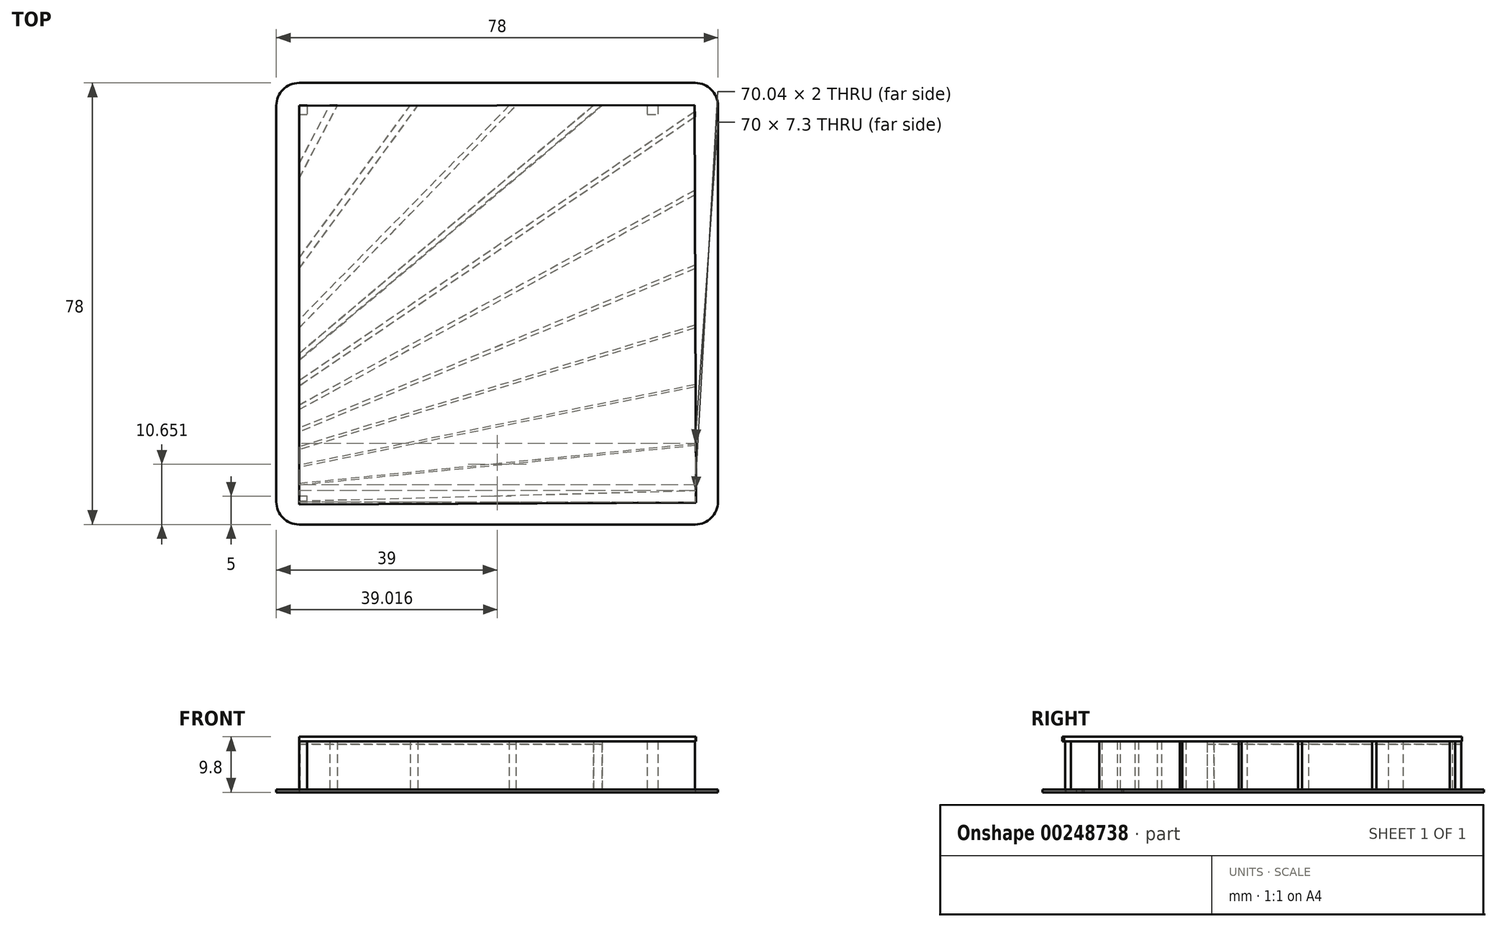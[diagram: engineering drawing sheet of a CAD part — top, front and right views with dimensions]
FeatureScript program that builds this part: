
annotation { "Feature Type Name" : "Feature", "Feature Type Description" : "" }
export const myFeature = defineFeature(function(context is Context, id is Id, definition is map)
    precondition{}
    {
        {
            var Q0;
            Q0=qCreatedBy(makeId("Top.planeOp"),FACE);
            var sketch = newSketch(context, id + "F0", { "sketchPlane" : qUnion([Q0])});
            skLineSegment(sketch, "E0.bottom", {"start": v(4, 78) * mm, "end": v(74, 78) * mm});
            skLineSegment(sketch, "E0.top", {"start": v(4, 0) * mm, "end": v(74, 0) * mm});
            skLineSegment(sketch, "E0.left", {"start": v(0, 74) * mm, "end": v(0, 4) * mm});
            skLineSegment(sketch, "E0.right", {"start": v(78, 74) * mm, "end": v(78, 4) * mm});
            skPoint(sketch, "E1.visualSharp", {"position": v(0, 0) * mm});
            skArc(sketch, "E1.filletArc", {"start": v(0, 4) * mm, "mid": v(1.17, 1.17) * mm, "end": v(4, 0) * mm});
            skPoint(sketch, "E2.visualSharp", {"position": v(0, 78) * mm});
            skArc(sketch, "E2.filletArc", {"start": v(4, 78) * mm, "mid": v(1.17, 76.83) * mm, "end": v(0, 74) * mm});
            skPoint(sketch, "E3.visualSharp", {"position": v(78, 0) * mm});
            skArc(sketch, "E3.filletArc", {"start": v(74, 0) * mm, "mid": v(76.83, 1.17) * mm, "end": v(78, 4) * mm});
            skPoint(sketch, "E4.visualSharp", {"position": v(78, 78) * mm});
            skArc(sketch, "E4.filletArc", {"start": v(78, 74) * mm, "mid": v(76.83, 76.83) * mm, "end": v(74, 78) * mm});
            skLineSegment(sketch, "E5.bottom", {"start": v(4, 4) * mm, "end": v(74.03, 4) * mm});
            skLineSegment(sketch, "E5.left", {"start": v(4, 4) * mm, "end": v(4, 4.15) * mm});
            skLineSegment(sketch, "E5.right", {"start": v(74.03, 4) * mm, "end": v(74, 6) * mm});
            skLineSegment(sketch, "E6", {"start": v(4, 4.15) * mm, "end": v(74, 6) * mm});
            skLineSegment(sketch, "E7", {"start": v(4, 7) * mm, "end": v(74, 14) * mm});
            skLineSegment(sketch, "E8", {"start": v(74.03, 4) * mm, "end": v(73.8, 70.2) * mm, "construction": true});
            skLineSegment(sketch, "E9", {"start": v(4, 4) * mm, "end": v(4, 69.95) * mm, "construction": true});
            skLineSegment(sketch, "E10.0", {"start": v(4, 7.3) * mm, "end": v(74, 14.3) * mm});
            skLineSegment(sketch, "E11", {"start": v(4, 7) * mm, "end": v(4, 7.3) * mm});
            skLineSegment(sketch, "E12", {"start": v(74, 14) * mm, "end": v(74, 14.3) * mm});
            skLineSegment(sketch, "E13", {"start": v(36.58, 10.26) * mm, "end": v(-29.54, 3.65) * mm});
            skLineSegment(sketch, "E14", {"start": v(74.03, 4) * mm, "end": v(-37.6, 3.62) * mm, "construction": true});
            skLineSegment(sketch, "E15", {"start": v(-9.34, 69.9) * mm, "end": v(86.2, 70.23) * mm});
            skSolve(sketch);
        }
        {
            var Q0;
            Q0 = qSketchRegion(id + "F0", true);
            extrude(context, id + "F1", {"entities" : qUnion([Q0]), "depth" : 0.5 * mm});
        }
        {
            var Q0;
            Q0=makeQuery(id+"F1.opExtrude","CAP_FACE",FACE,{"disambiguationData":[OSD([sQuery(id+"F0.wireOp",EDGE,"E0.bottom"),sQuery(id+"F0.wireOp",EDGE,"E0.top"),sQuery(id+"F0.wireOp",EDGE,"E0.left"),sQuery(id+"F0.wireOp",EDGE,"E0.right"),sQuery(id+"F0.wireOp",EDGE,"E1.filletArc"),sQuery(id+"F0.wireOp",EDGE,"E2.filletArc"),sQuery(id+"F0.wireOp",EDGE,"E3.filletArc"),sQuery(id+"F0.wireOp",EDGE,"E4.filletArc"),sQuery(id+"F0.wireOp",EDGE,"E5.bottom"),sQuery(id+"F0.wireOp",EDGE,"E5.left"),sQuery(id+"F0.wireOp",EDGE,"E5.right"),sQuery(id+"F0.wireOp",EDGE,"E6"),sQuery(id+"F0.wireOp",EDGE,"E7"),sQuery(id+"F0.wireOp",EDGE,"E10.0"),sQuery(id+"F0.wireOp",EDGE,"E11"),sQuery(id+"F0.wireOp",EDGE,"E12"),sQuery(id+"F0.wireOp",EDGE,"E13")])],"isStart":false});
            var sketch = newSketch(context, id + "F2", { "sketchPlane" : qUnion([Q0])});
            skLineSegment(sketch, "E16", {"start": v(73.96, 24.3) * mm, "end": v(4, 10.1) * mm});
            skLineSegment(sketch, "E17", {"start": v(73.96, 34.7) * mm, "end": v(4, 13.21) * mm});
            skLineSegment(sketch, "E18", {"start": v(73.96, 45.2) * mm, "end": v(4, 16.36) * mm});
            skLineSegment(sketch, "E19", {"start": v(73.96, 58.23) * mm, "end": v(4, 20.28) * mm});
            skLineSegment(sketch, "E20", {"start": v(73.96, 71.98) * mm, "end": v(4, 24.4) * mm});
            skLineSegment(sketch, "E21", {"start": v(57.55, 74) * mm, "end": v(4, 29.13) * mm});
            skLineSegment(sketch, "E22.0", {"start": v(73.96, 24.7) * mm, "end": v(4, 10.5) * mm});
            skLineSegment(sketch, "E23", {"start": v(4, 10.5) * mm, "end": v(4, 10.1) * mm});
            skLineSegment(sketch, "E24.0", {"start": v(73.96, 35.22) * mm, "end": v(4, 13.74) * mm});
            skLineSegment(sketch, "E25", {"start": v(4, 13.74) * mm, "end": v(4, 13.21) * mm});
            skLineSegment(sketch, "E26.trimOffspring", {"start": v(4, 13.21) * mm, "end": v(4, 13.74) * mm});
            skLineSegment(sketch, "E27", {"start": v(73.96, 34.7) * mm, "end": v(73.96, 35.22) * mm});
            skLineSegment(sketch, "E28.0", {"start": v(73.96, 45.85) * mm, "end": v(4, 17.01) * mm});
            skLineSegment(sketch, "E29", {"start": v(73.96, 45.2) * mm, "end": v(73.96, 45.85) * mm});
            skLineSegment(sketch, "E30", {"start": v(4, 16.36) * mm, "end": v(4, 17.01) * mm});
            skLineSegment(sketch, "E31.0", {"start": v(73.96, 59.03) * mm, "end": v(4, 21.07) * mm});
            skLineSegment(sketch, "E32.0", {"start": v(73.97, 72.95) * mm, "end": v(4, 25.37) * mm});
            skLineSegment(sketch, "E33", {"start": v(73.96, 71.98) * mm, "end": v(73.97, 72.95) * mm});
            skLineSegment(sketch, "E34", {"start": v(4, 25.37) * mm, "end": v(4, 24.4) * mm});
            skLineSegment(sketch, "E35.0", {"start": v(56.15, 74) * mm, "end": v(4, 30.3) * mm});
            skLineSegment(sketch, "E36.trimOffspring", {"start": v(4, 34.73) * mm, "end": v(42.33, 74) * mm});
            skLineSegment(sketch, "E37", {"start": v(4, 36.17) * mm, "end": v(4, 34.73) * mm});
            skLineSegment(sketch, "E38", {"start": v(42.33, 74) * mm, "end": v(41.14, 74) * mm});
            skLineSegment(sketch, "E39", {"start": v(41.14, 74) * mm, "end": v(4, 36.17) * mm});
            skLineSegment(sketch, "E40", {"start": v(4, 45.17) * mm, "end": v(25, 74) * mm});
            skLineSegment(sketch, "E41.0", {"start": v(4, 47.04) * mm, "end": v(23.64, 74) * mm});
            skLineSegment(sketch, "E42.trimOffspring", {"start": v(32.02, 85.5) * mm, "end": v(32.02, 85.5) * mm});
            skLineSegment(sketch, "E43", {"start": v(4, 61.13) * mm, "end": v(10.76, 74) * mm});
            skLineSegment(sketch, "E44.0", {"start": v(4, 63.7) * mm, "end": v(9.4, 74) * mm});
            skLineSegment(sketch, "E45.trimOffspring", {"start": v(19.44, 93.12) * mm, "end": v(19.45, 93.12) * mm});
            skLineSegment(sketch, "E46.bottom", {"start": v(4, 74) * mm, "end": v(5.42, 74) * mm});
            skLineSegment(sketch, "E46.top", {"start": v(4, 72.42) * mm, "end": v(5.42, 72.42) * mm});
            skLineSegment(sketch, "E46.left", {"start": v(4, 74) * mm, "end": v(4, 72.42) * mm});
            skLineSegment(sketch, "E46.right", {"start": v(5.42, 74) * mm, "end": v(5.42, 72.42) * mm});
            skLineSegment(sketch, "E47.bottom", {"start": v(65.51, 74) * mm, "end": v(67.4, 74) * mm});
            skLineSegment(sketch, "E47.top", {"start": v(65.51, 72.42) * mm, "end": v(67.4, 72.42) * mm});
            skLineSegment(sketch, "E47.left", {"start": v(65.51, 74) * mm, "end": v(65.51, 72.42) * mm});
            skLineSegment(sketch, "E47.right", {"start": v(67.4, 74) * mm, "end": v(67.4, 72.42) * mm});
            skLineSegment(sketch, "E48.bottom", {"start": v(4, 4) * mm, "end": v(5.42, 4) * mm});
            skLineSegment(sketch, "E48.top", {"start": v(4, 5.04) * mm, "end": v(5.42, 5.04) * mm});
            skLineSegment(sketch, "E48.left", {"start": v(4, 4) * mm, "end": v(4, 5.04) * mm});
            skLineSegment(sketch, "E48.right", {"start": v(5.42, 4) * mm, "end": v(5.42, 5.04) * mm});
            skLineSegment(sketch, "E49", {"start": v(4, 63.7) * mm, "end": v(4, 61.13) * mm});
            skLineSegment(sketch, "E50", {"start": v(4, 47.04) * mm, "end": v(4, 45.17) * mm});
            skLineSegment(sketch, "E51", {"start": v(4, 30.3) * mm, "end": v(4, 29.13) * mm});
            skLineSegment(sketch, "E52", {"start": v(4, 21.07) * mm, "end": v(4, 20.28) * mm});
            skLineSegment(sketch, "E53", {"start": v(9.4, 74) * mm, "end": v(10.76, 74) * mm});
            skLineSegment(sketch, "E54", {"start": v(23.64, 74) * mm, "end": v(25, 74) * mm});
            skLineSegment(sketch, "E55", {"start": v(56.14, 74) * mm, "end": v(57.54, 73.98) * mm});
            skLineSegment(sketch, "E56", {"start": v(73.96, 59.03) * mm, "end": v(73.96, 58.23) * mm});
            skLineSegment(sketch, "E57", {"start": v(73.96, 24.7) * mm, "end": v(73.96, 24.3) * mm});
            skSolve(sketch);
        }
        {
            var Q0;
            Q0 = qSketchRegion(id + "F2", true);
            extrude(context, id + "F3", {"entities" : qUnion([Q0]), "depth" : 8.5 * mm});
        }
        {
            var Q0;
            Q0=qCreatedBy(makeId("Top.planeOp"),FACE);
            var sketch = newSketch(context, id + "F4", { "sketchPlane" : qUnion([Q0])});
            skLineSegment(sketch, "E58", {"start": v(4.06, 30.3) * mm, "end": v(4.06, 29.14) * mm});
            skLineSegment(sketch, "E59", {"start": v(4.06, 29.14) * mm, "end": v(57.47, 74.03) * mm});
            skLineSegment(sketch, "E60", {"start": v(57.47, 74.03) * mm, "end": v(55.98, 74.03) * mm});
            skLineSegment(sketch, "E61", {"start": v(55.98, 74.03) * mm, "end": v(4.06, 30.3) * mm});
            skSolve(sketch);
        }
        {
            var Q0;
            Q0 = qSketchRegion(id + "F4", true);
            extrude(context, id + "F5", {"entities" : qUnion([Q0]), "operationType" : NewBodyOperationType.ADD, "depth" : 8.5 * mm});
        }
        {
            var Q0;
            Q0 = qSketchRegion(id + "F4", true);
            var Q1;
            Q1 = qSketchRegion(id + "F7", true);
            extrude(context, id + "F6", {"entities" : qUnion([Q0, Q1]), "depth" : 8.5 * mm});
        }
        {
            var Q0;
            Q0=makeQuery(id+"F3.opExtrude","CAP_FACE",FACE,{"disambiguationData":[OSD([sQuery(id+"F2.wireOp",EDGE,"E43"),sQuery(id+"F2.wireOp",EDGE,"E44.0"),sQuery(id+"F2.wireOp",EDGE,"E49"),sQuery(id+"F2.wireOp",EDGE,"E53")])],"isStart":false});
            var sketch = newSketch(context, id + "F7", { "sketchPlane" : qUnion([Q0])});
            skLineSegment(sketch, "E62", {"start": v(4.01, 3.55) * mm, "end": v(4.01, 73.98) * mm});
            skLineSegment(sketch, "E63", {"start": v(74.16, 3.84) * mm, "end": v(4.01, 3.55) * mm});
            skLineSegment(sketch, "E64", {"start": v(74.16, 3.84) * mm, "end": v(73.89, 74.1) * mm});
            skLineSegment(sketch, "E65", {"start": v(4.01, 73.98) * mm, "end": v(73.89, 74.1) * mm});
            skSolve(sketch);
        }
        {
            var Q0;
            Q0 = qSketchRegion(id + "F7", true);
            var Q1;
            Q1=sQuery(id+"F7.wireOp",EDGE,"E63");
            var Q2;
            Q2=sQuery(id+"F7.wireOp",EDGE,"E64");
            var Q3;
            Q3=sQuery(id+"F7.wireOp",EDGE,"E65");
            var Q4;
            Q4=sQuery(id+"F7.wireOp",EDGE,"E62");
            extrude(context, id + "F8", {"entities" : qUnion([Q0]), "operationType" : NewBodyOperationType.ADD, "surfaceEntities" : qUnion([Q1, Q2, Q3, Q4]), "depth" : 0.8 * mm});
        }
        {
            var Q0;
            Q0=makeQuery(id+"F6.opExtrude","SWEPT_BODY",BODY,{"disambiguationData":[OSD([sQuery(id+"F4.wireOp",EDGE,"E58"),sQuery(id+"F4.wireOp",EDGE,"E59"),sQuery(id+"F4.wireOp",EDGE,"E60"),sQuery(id+"F4.wireOp",EDGE,"E61")])]});
            var Q1;
            Q1=makeQuery(id+"F6.opExtrude","CAP_VERTEX",VERTEX,{"disambiguationData":[OSD([sQuery(id+"F4.wireOp",EDGE,"E59"),sQuery(id+"F4.wireOp",EDGE,"E60")])],"isStart":true});
            var Q2;
            Q2=sQuery(id+"F2.wireOp",VERTEX,"E21.start");
            transform(context, id + "F9", {"entities" : qUnion([Q0]), "transformType" : TransformType.TRANSLATION_DISTANCE, "transformDirection" : qUnion([Q1, Q2]), "distance" : 0.5 * mm, "makeCopy" : false});
        }
        {
            var Q0;
            Q0=sQuery(id+"F0.wireOp",EDGE,"E5.bottom");
            var Q1;
            Q1=sQuery(id+"F0.wireOp",EDGE,"E10.0");
            var Q2;
            Q2=sQuery(id+"F0.wireOp",EDGE,"E7");
            var Q3;
            Q3=sQuery(id+"F0.wireOp",EDGE,"E6");
            var Q4;
            Q4=sQuery(id+"F0.wireOp",EDGE,"E5.right");
            var Q5;
            Q5=sQuery(id+"F0.wireOp",EDGE,"E11");
            var Q6;
            Q6=sQuery(id+"F0.wireOp",EDGE,"E12");
            var Q7;
            Q7=sQuery(id+"F0.wireOp",EDGE,"E5.left");
            extrude(context, id + "F10", {"bodyType" : ToolBodyType.SURFACE, "surfaceEntities" : qUnion([Q0, Q1, Q2, Q3, Q4, Q5, Q6, Q7]), "depth" : 8.5 * mm});
        }
    });
